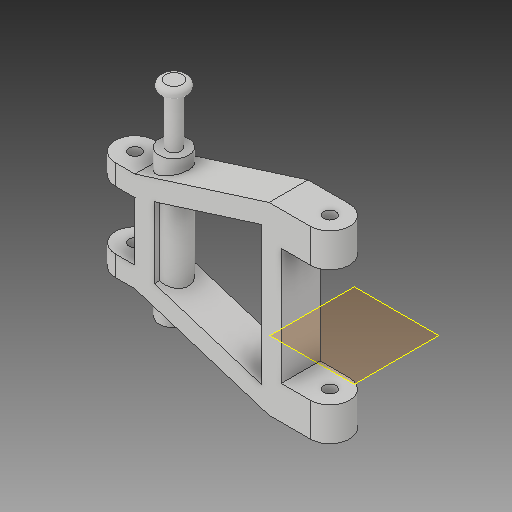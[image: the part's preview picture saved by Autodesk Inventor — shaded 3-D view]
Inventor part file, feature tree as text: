
AUTODESK INVENTOR PART (.ipt)
format: ipt  version: 2019 (Build 230136000, 136)  size: 181,760 bytes
history: native  units: in
note: dims shown in document units (in); Inventor stores cm internally (conversion verified against a paired STEP export)
features: sketch x4, other x3, plane x1
ambient origin geometry x8: Origin, YZ Plane, XZ Plane, XY Plane, X Axis, Y Axis, Z Axis, Center Point
bodies: Solid1 (feature_tree)
feature tree (8):
  other  "A_Arm_MIR.ipt"
  other  "Solid1::A_Arm_MIR.ipt"
  other  "TaggingFeature1"
  sketch  "Sketch2"  dims[d0=0.3937in]
  sketch  "Sketch3"
  sketch  "Sketch4"
  sketch  "Sketch5"
  plane  "Work Plane1"
